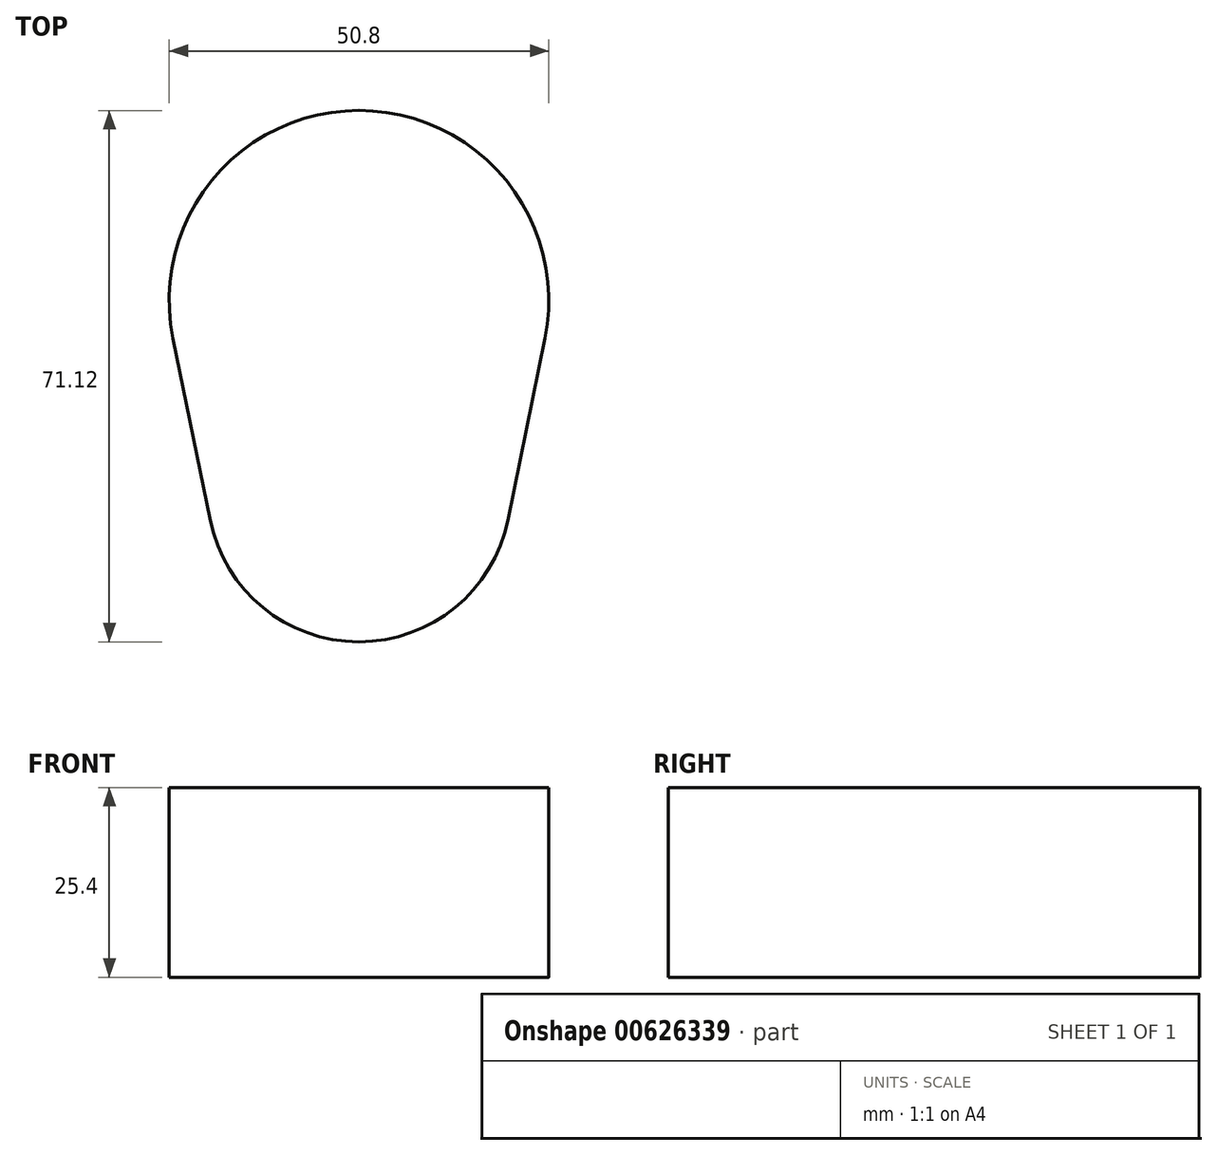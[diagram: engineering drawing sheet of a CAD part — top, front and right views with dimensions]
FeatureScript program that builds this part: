
annotation { "Feature Type Name" : "Feature", "Feature Type Description" : "" }
export const myFeature = defineFeature(function(context is Context, id is Id, definition is map)
    precondition{}
    {
        {
            var Q0;
            Q0=qCreatedBy(makeId("Top.planeOp"),FACE);
            var sketch = newSketch(context, id + "F0", { "sketchPlane" : qUnion([Q0])});
            skLineSegment(sketch, "E0", {"start": v(19.9, -4.06) * mm, "end": v(24.89, 20.32) * mm});
            skArc(sketch, "E1", {"start": v(24.89, 20.32) * mm, "mid": v(0, 50.8) * mm, "end": v(-24.89, 20.32) * mm});
            skLineSegment(sketch, "E2", {"start": v(-24.89, 20.32) * mm, "end": v(-19.9, -4.06) * mm});
            skArc(sketch, "E3", {"start": v(-19.9, -4.06) * mm, "mid": v(0, -20.32) * mm, "end": v(19.9, -4.06) * mm});
            skSolve(sketch);
        }
        {
            var Q0;
            Q0 = qSketchRegion(id + "F0", true);
            extrude(context, id + "F1", {"entities" : qUnion([Q0]), "depth" : 25.4 * mm, "offsetDistance" : 25.4 * mm});
        }
    });
